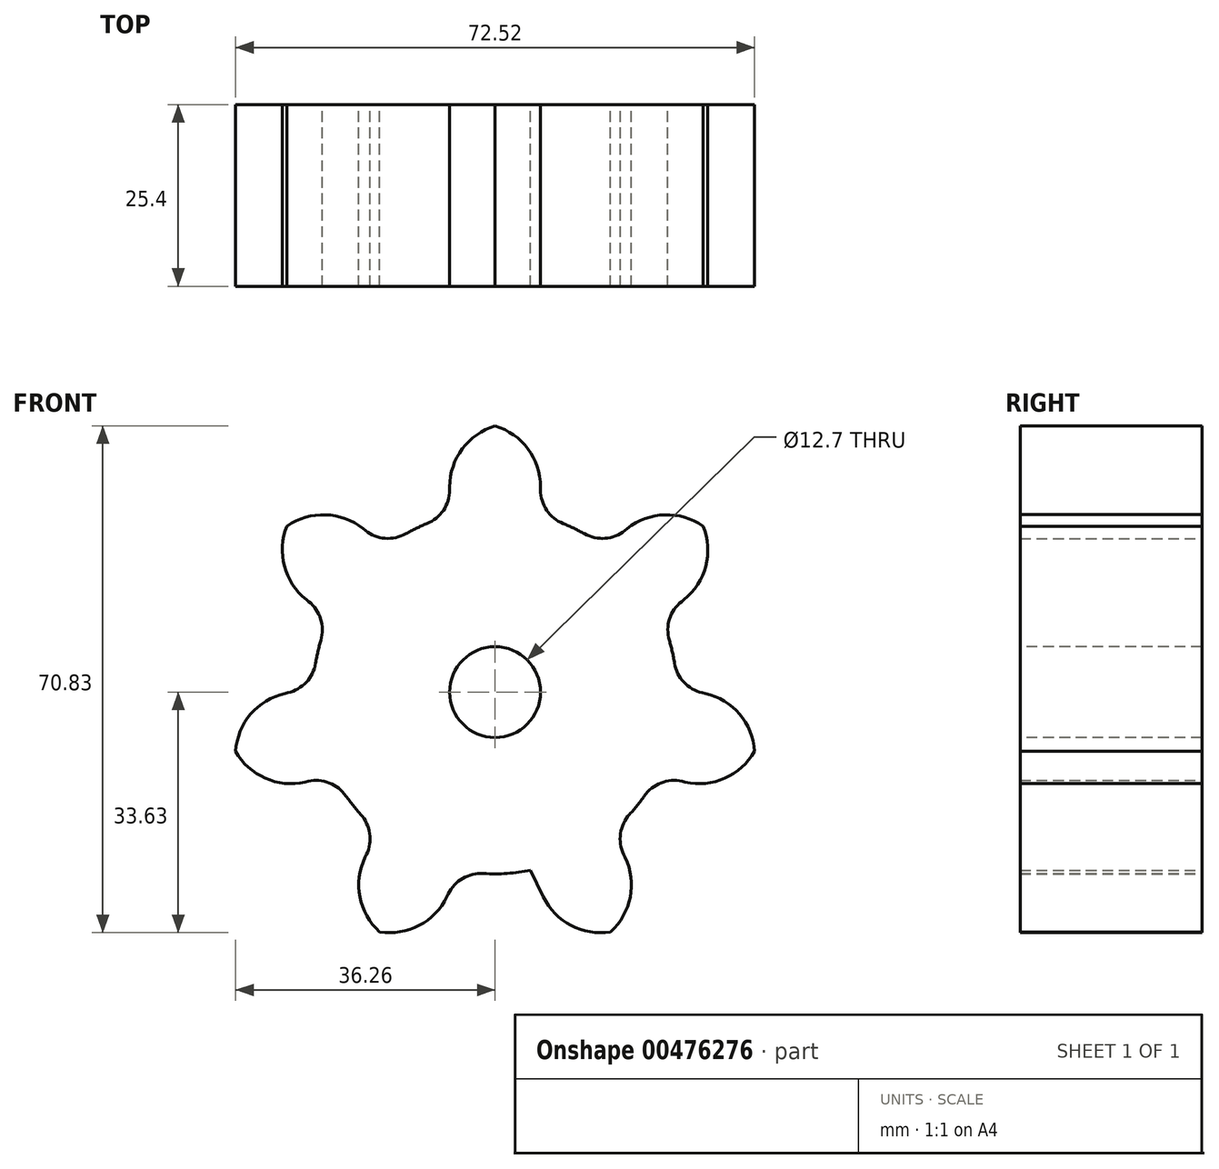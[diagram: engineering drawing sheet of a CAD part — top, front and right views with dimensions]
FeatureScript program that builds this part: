
annotation { "Feature Type Name" : "Feature", "Feature Type Description" : "" }
export const myFeature = defineFeature(function(context is Context, id is Id, definition is map)
    precondition{}
    {
        {
            var Q0;
            Q0=qCreatedBy(makeId("Front.planeOp"),FACE);
            var sketch = newSketch(context, id + "F0", { "sketchPlane" : qUnion([Q0])});
            skCircle(sketch, "E0", {"center": v(0, 0) * mm, "radius": 6.35 * mm});
            skCircle(sketch, "E1", {"center": v(0, 0) * mm, "radius": 25.4 * mm});
            skCircle(sketch, "E2", {"center": v(0, 0) * mm, "radius": 38.1 * mm, "construction": true});
            skLineSegment(sketch, "E3.bottom", {"start": v(-6.35, 37.57) * mm, "end": v(6.35, 37.57) * mm});
            skLineSegment(sketch, "E3.top", {"start": v(-6.35, -37.57) * mm, "end": v(6.35, -37.57) * mm});
            skLineSegment(sketch, "E4", {"start": v(25.41, 28.39) * mm, "end": v(33.33, 18.46) * mm});
            skLineSegment(sketch, "E5", {"start": v(-27.13, -26.75) * mm, "end": v(-34.42, -16.35) * mm});
            skPoint(sketch, "E6.startSnap0", {"position": v(-6.35, 0) * mm});
            skLineSegment(sketch, "E7", {"start": v(-8.92, 1) * mm, "end": v(-1, -8.92) * mm});
            skLineSegment(sketch, "E8", {"start": v(-8.92, 1) * mm, "end": v(25.41, 28.39) * mm});
            skLineSegment(sketch, "E9", {"start": v(-1, -8.92) * mm, "end": v(33.33, 18.46) * mm});
            skLineSegment(sketch, "E10", {"start": v(-6.35, -6.35) * mm, "end": v(6.35, -6.35) * mm});
            skLineSegment(sketch, "E11", {"start": v(6.35, -6.35) * mm, "end": v(6.35, 37.57) * mm});
            skLineSegment(sketch, "E12", {"start": v(-6.35, 37.57) * mm, "end": v(-6.35, -6.35) * mm});
            skLineSegment(sketch, "E13", {"start": v(-4.78, 7.6) * mm, "end": v(38.04, -2.17) * mm});
            skLineSegment(sketch, "E14", {"start": v(38.04, -2.17) * mm, "end": v(35.21, -14.55) * mm});
            skLineSegment(sketch, "E15", {"start": v(35.21, -14.55) * mm, "end": v(-7.6, -4.78) * mm});
            skLineSegment(sketch, "E16", {"start": v(-7.6, -4.78) * mm, "end": v(-4.78, 7.6) * mm});
            skSolve(sketch);
        }
        {
            var Q0;
            Q0=qCreatedBy(makeId("Front.planeOp"),FACE);
            var sketch = newSketch(context, id + "F1", { "sketchPlane" : qUnion([Q0])});
            skCircle(sketch, "E17", {"center": v(0, 0) * mm, "radius": 6.35 * mm});
            skCircle(sketch, "E18", {"center": v(0, 0) * mm, "radius": 38.1 * mm, "construction": true});
            skLineSegment(sketch, "E19", {"start": v(-7.05, 0) * mm, "end": v(10.58, -36.6) * mm});
            skLineSegment(sketch, "E20", {"start": v(10.58, -36.6) * mm, "end": v(22.02, -31.1) * mm});
            skLineSegment(sketch, "E21", {"start": v(22.02, -31.1) * mm, "end": v(2.97, 8.48) * mm});
            skLineSegment(sketch, "E22", {"start": v(2.97, 8.48) * mm, "end": v(-8.48, 2.97) * mm});
            skLineSegment(sketch, "E23", {"start": v(-8.48, 2.97) * mm, "end": v(10.58, -36.6) * mm});
            skLineSegment(sketch, "E24", {"start": v(9.16, 4.38) * mm, "end": v(-10.58, -36.6) * mm});
            skLineSegment(sketch, "E25", {"start": v(-10.58, -36.6) * mm, "end": v(-22.02, -31.1) * mm});
            skLineSegment(sketch, "E26", {"start": v(-22.02, -31.1) * mm, "end": v(-2.97, 8.48) * mm});
            skLineSegment(sketch, "E27", {"start": v(-2.97, 8.48) * mm, "end": v(8.48, 2.97) * mm});
            skLineSegment(sketch, "E28", {"start": v(15.16, -3.05) * mm, "end": v(-35.21, -14.55) * mm});
            skLineSegment(sketch, "E29", {"start": v(-35.21, -14.55) * mm, "end": v(-38.04, -2.17) * mm});
            skLineSegment(sketch, "E30", {"start": v(-38.04, -2.17) * mm, "end": v(12.96, 9.47) * mm});
            skLineSegment(sketch, "E31", {"start": v(12.96, 9.47) * mm, "end": v(15.16, -3.05) * mm});
            skLineSegment(sketch, "E32", {"start": v(12.08, -1.5) * mm, "end": v(-25.41, 28.39) * mm});
            skLineSegment(sketch, "E33", {"start": v(-25.41, 28.39) * mm, "end": v(-33.33, 18.46) * mm});
            skLineSegment(sketch, "E34", {"start": v(-33.33, 18.46) * mm, "end": v(3.34, -10.79) * mm});
            skLineSegment(sketch, "E35", {"start": v(3.34, -10.79) * mm, "end": v(12.08, -1.5) * mm});
            skSolve(sketch);
        }
        {
            var Q0;
            {var subQ5=sQuery(id+"F0.wireOp",EDGE,"E4");Q0=makeQuery(id+"F0.imprint","IMPRINT",FACE,{"disambiguationData":[TD([[makeQuery(id+"F0.imprint","IMPRINT",EDGE,{"derivedFrom":subQ5}),-1.0]])]});}
            var Q1;
            {var subQ5=sQuery(id+"F0.wireOp",EDGE,"E3.bottom");Q1=makeQuery(id+"F0.imprint","IMPRINT",FACE,{"disambiguationData":[TD([[makeQuery(id+"F0.imprint","IMPRINT",EDGE,{"derivedFrom":subQ5}),-1.0]])]});}
            var Q2;
            {var subQ5=sQuery(id+"F0.wireOp",EDGE,"E14");Q2=makeQuery(id+"F0.imprint","IMPRINT",FACE,{"disambiguationData":[TD([[makeQuery(id+"F0.imprint","IMPRINT",EDGE,{"derivedFrom":subQ5}),-1.0]])]});}
            var Q3;
            {var subQ0=sQuery(id+"F0.wireOp",EDGE,"E9");var subQ1=sQuery(id+"F0.wireOp",EDGE,"E1");var subQ2=makeQuery(id+"F0.imprint","INTERSECT",VERTEX,{"derivedFrom":[subQ1,subQ0]});Q3=makeQuery(id+"F0.imprint","IMPRINT",FACE,{"disambiguationData":[TD([[makeQuery(id+"F0.imprint","IMPRINT",EDGE,{"disambiguationData":[TD([[subQ2,1.0]])],"derivedFrom":subQ1}),1.0]])]});}
            var Q4;
            {var subQ0=sQuery(id+"F0.wireOp",EDGE,"E8");var subQ1=sQuery(id+"F0.wireOp",EDGE,"E1");var subQ2=makeQuery(id+"F0.imprint","INTERSECT",VERTEX,{"derivedFrom":[subQ1,subQ0]});Q4=makeQuery(id+"F0.imprint","IMPRINT",FACE,{"disambiguationData":[TD([[makeQuery(id+"F0.imprint","IMPRINT",EDGE,{"disambiguationData":[TD([[subQ2,-1.0]])],"derivedFrom":subQ1}),1.0]])]});}
            var Q5;
            {var subQ1=sQuery(id+"F0.wireOp",EDGE,"E1");var subQ7=sQuery(id+"F0.wireOp",EDGE,"E9");var subQ8=makeQuery(id+"F0.imprint","INTERSECT",VERTEX,{"derivedFrom":[subQ1,subQ7]});Q5=makeQuery(id+"F0.imprint","IMPRINT",FACE,{"disambiguationData":[TD([[makeQuery(id+"F0.imprint","IMPRINT",EDGE,{"disambiguationData":[TD([[subQ8,-1.0]])],"derivedFrom":subQ1}),1.0]])]});}
            var Q6;
            {var subQ0=sQuery(id+"F0.wireOp",EDGE,"E11");var subQ1=sQuery(id+"F0.wireOp",EDGE,"E1");var subQ2=makeQuery(id+"F0.imprint","INTERSECT",VERTEX,{"derivedFrom":[subQ1,subQ0]});Q6=makeQuery(id+"F0.imprint","IMPRINT",FACE,{"disambiguationData":[TD([[makeQuery(id+"F0.imprint","IMPRINT",EDGE,{"disambiguationData":[TD([[subQ2,-1.0]])],"derivedFrom":subQ1}),1.0]])]});}
            var Q7;
            {var subQ0=sQuery(id+"F0.wireOp",EDGE,"E12");var subQ5=sQuery(id+"F0.wireOp",EDGE,"E1");var subQ6=makeQuery(id+"F0.imprint","INTERSECT",VERTEX,{"derivedFrom":[subQ5,subQ0]});Q7=makeQuery(id+"F0.imprint","IMPRINT",FACE,{"disambiguationData":[TD([[makeQuery(id+"F0.imprint","IMPRINT",EDGE,{"disambiguationData":[TD([[subQ6,-1.0]])],"derivedFrom":subQ5}),1.0]])]});}
            var Q8;
            {var subQ6=sQuery(id+"F0.wireOp",EDGE,"E1");var subQ10=sQuery(id+"F0.wireOp",EDGE,"E13");var subQ12=makeQuery(id+"F0.imprint","INTERSECT",VERTEX,{"derivedFrom":[subQ6,subQ10]});Q8=makeQuery(id+"F0.imprint","IMPRINT",FACE,{"disambiguationData":[TD([[makeQuery(id+"F0.imprint","IMPRINT",EDGE,{"disambiguationData":[TD([[subQ12,1.0]])],"derivedFrom":subQ6}),1.0]])]});}
            var Q9;
            Q9=makeQuery(id+"F3.opExtrude","SWEPT_FACE",FACE,{"disambiguationData":[OSD([sQuery(id+"F1.wireOp",EDGE,"E31")])]});
            var Q10;
            Q10=makeQuery(id+"F3.opExtrude","SWEPT_FACE",FACE,{"disambiguationData":[OSD([sQuery(id+"F1.wireOp",EDGE,"E29")])]});
            var Q11;
            {var subQ0=sQuery(id+"F1.wireOp",EDGE,"E28");Q11=makeQuery(id+"F3.opExtrude","SWEPT_FACE",FACE,{"disambiguationData":[OSD([subQ0]),TDD([makeQuery(id+"F1.imprint","IMPRINT",EDGE,{"disambiguationData":[TD([[makeQuery(id+"F1.imprint","INTERSECT",VERTEX,{"derivedFrom":[subQ0,sQuery(id+"F1.wireOp",EDGE,"E29")]}),1.0]])],"derivedFrom":subQ0})])]});}
            var Q12;
            {var subQ0=sQuery(id+"F1.wireOp",EDGE,"E23");Q12=makeQuery(id+"F3.opExtrude","SWEPT_FACE",FACE,{"disambiguationData":[OSD([subQ0]),TDD([makeQuery(id+"F1.imprint","IMPRINT",EDGE,{"disambiguationData":[TD([[makeQuery(id+"F1.imprint","INTERSECT",VERTEX,{"derivedFrom":[sQuery(id+"F1.wireOp",EDGE,"E20"),subQ0]}),1.0]])],"derivedFrom":subQ0})])]});}
            var Q13;
            {var subQ0=sQuery(id+"F1.wireOp",EDGE,"E21");Q13=makeQuery(id+"F3.opExtrude","SWEPT_FACE",FACE,{"disambiguationData":[OSD([subQ0]),TDD([makeQuery(id+"F1.imprint","IMPRINT",EDGE,{"disambiguationData":[TD([[makeQuery(id+"F1.imprint","INTERSECT",VERTEX,{"derivedFrom":[sQuery(id+"F1.wireOp",EDGE,"E20"),subQ0]}),-1.0]])],"derivedFrom":subQ0})])]});}
            var Q14;
            Q14=makeQuery(id+"F3.opExtrude","CAP_FACE",FACE,{"disambiguationData":[OSD([sQuery(id+"F1.wireOp",EDGE,"E20"),sQuery(id+"F1.wireOp",EDGE,"E21"),sQuery(id+"F1.wireOp",EDGE,"E22"),sQuery(id+"F1.wireOp",EDGE,"E23"),sQuery(id+"F1.wireOp",EDGE,"E24"),sQuery(id+"F1.wireOp",EDGE,"E25"),sQuery(id+"F1.wireOp",EDGE,"E26"),sQuery(id+"F1.wireOp",EDGE,"E27"),sQuery(id+"F1.wireOp",EDGE,"E28"),sQuery(id+"F1.wireOp",EDGE,"E29"),sQuery(id+"F1.wireOp",EDGE,"E30"),sQuery(id+"F1.wireOp",EDGE,"E31"),sQuery(id+"F1.wireOp",EDGE,"E32"),sQuery(id+"F1.wireOp",EDGE,"E33"),sQuery(id+"F1.wireOp",EDGE,"E34"),sQuery(id+"F1.wireOp",EDGE,"E35")])],"isStart":false});
            var Q15;
            {var subQ0=sQuery(id+"F1.wireOp",EDGE,"E28");Q15=makeQuery(id+"F3.opExtrude","SWEPT_FACE",FACE,{"disambiguationData":[OSD([subQ0]),TDD([makeQuery(id+"F1.imprint","IMPRINT",EDGE,{"disambiguationData":[TD([[makeQuery(id+"F1.imprint","INTERSECT",VERTEX,{"derivedFrom":[subQ0,sQuery(id+"F1.wireOp",EDGE,"E31")]}),-1.0]])],"derivedFrom":subQ0})])]});}
            var Q16;
            Q16=makeQuery(id+"F3.opExtrude","CAP_FACE",FACE,{"disambiguationData":[OSD([sQuery(id+"F1.wireOp",EDGE,"E20"),sQuery(id+"F1.wireOp",EDGE,"E21"),sQuery(id+"F1.wireOp",EDGE,"E22"),sQuery(id+"F1.wireOp",EDGE,"E23"),sQuery(id+"F1.wireOp",EDGE,"E24"),sQuery(id+"F1.wireOp",EDGE,"E25"),sQuery(id+"F1.wireOp",EDGE,"E26"),sQuery(id+"F1.wireOp",EDGE,"E27"),sQuery(id+"F1.wireOp",EDGE,"E28"),sQuery(id+"F1.wireOp",EDGE,"E29"),sQuery(id+"F1.wireOp",EDGE,"E30"),sQuery(id+"F1.wireOp",EDGE,"E31"),sQuery(id+"F1.wireOp",EDGE,"E32"),sQuery(id+"F1.wireOp",EDGE,"E33"),sQuery(id+"F1.wireOp",EDGE,"E34"),sQuery(id+"F1.wireOp",EDGE,"E35")])],"isStart":true});
            var Q17;
            Q17=makeQuery(id+"F3.opExtrude","SWEPT_FACE",FACE,{"disambiguationData":[OSD([sQuery(id+"F1.wireOp",EDGE,"E20")])]});
            var Q18;
            Q18=makeQuery(id+"F3.opExtrude","SWEPT_FACE",FACE,{"disambiguationData":[OSD([sQuery(id+"F1.wireOp",EDGE,"E25")])]});
            var Q19;
            {var subQ0=sQuery(id+"F1.wireOp",EDGE,"E24");Q19=makeQuery(id+"F3.opExtrude","SWEPT_FACE",FACE,{"disambiguationData":[OSD([subQ0]),TDD([makeQuery(id+"F1.imprint","IMPRINT",EDGE,{"disambiguationData":[TD([[makeQuery(id+"F1.imprint","INTERSECT",VERTEX,{"derivedFrom":[subQ0,sQuery(id+"F1.wireOp",EDGE,"E25")]}),1.0]])],"derivedFrom":subQ0})])]});}
            var Q20;
            {var subQ0=sQuery(id+"F1.wireOp",EDGE,"E26");Q20=makeQuery(id+"F3.opExtrude","SWEPT_FACE",FACE,{"disambiguationData":[OSD([subQ0]),TDD([makeQuery(id+"F1.imprint","IMPRINT",EDGE,{"disambiguationData":[TD([[makeQuery(id+"F1.imprint","INTERSECT",VERTEX,{"derivedFrom":[sQuery(id+"F1.wireOp",EDGE,"E25"),subQ0]}),-1.0]])],"derivedFrom":subQ0})])]});}
            var Q21;
            {var subQ0=sQuery(id+"F0.wireOp",EDGE,"E13");var subQ1=sQuery(id+"F0.wireOp",EDGE,"E0");var subQ2=makeQuery(id+"F0.imprint","INTERSECT",VERTEX,{"derivedFrom":[subQ1,subQ0]});Q21=makeQuery(id+"F0.imprint","IMPRINT",FACE,{"disambiguationData":[TD([[makeQuery(id+"F0.imprint","IMPRINT",EDGE,{"disambiguationData":[TD([[subQ2,-1.0]])],"derivedFrom":subQ1}),-1.0]])]});}
            var Q22;
            {var subQ0=sQuery(id+"F0.wireOp",EDGE,"E8");var subQ1=makeQuery(id+"F0.imprint","INTERSECT",VERTEX,{"derivedFrom":[sQuery(id+"F0.wireOp",EDGE,"E0"),subQ0]});Q22=makeQuery(id+"F0.imprint","IMPRINT",FACE,{"disambiguationData":[TD([[makeQuery(id+"F0.imprint","IMPRINT",EDGE,{"disambiguationData":[TD([[subQ1,1.0]])],"derivedFrom":subQ0}),1.0]])]});}
            var Q23;
            {var subQ0=sQuery(id+"F0.wireOp",EDGE,"E11");var subQ1=sQuery(id+"F0.wireOp",EDGE,"E9");var subQ2=makeQuery(id+"F0.imprint","INTERSECT",VERTEX,{"derivedFrom":[subQ1,subQ0]});Q23=makeQuery(id+"F0.imprint","IMPRINT",FACE,{"disambiguationData":[TD([[makeQuery(id+"F0.imprint","IMPRINT",EDGE,{"disambiguationData":[TD([[subQ2,-1.0]])],"derivedFrom":subQ1}),1.0]])]});}
            var Q24;
            {var subQ0=sQuery(id+"F1.wireOp",EDGE,"E30");Q24=makeQuery(id+"F3.opExtrude","SWEPT_FACE",FACE,{"disambiguationData":[OSD([subQ0]),TDD([makeQuery(id+"F1.imprint","IMPRINT",EDGE,{"disambiguationData":[TD([[makeQuery(id+"F1.imprint","INTERSECT",VERTEX,{"derivedFrom":[subQ0,sQuery(id+"F1.wireOp",EDGE,"E31")]}),1.0]])],"derivedFrom":subQ0})])]});}
            var Q25;
            {var subQ0=sQuery(id+"F1.wireOp",EDGE,"E30");Q25=makeQuery(id+"F3.opExtrude","SWEPT_FACE",FACE,{"disambiguationData":[OSD([subQ0]),TDD([makeQuery(id+"F1.imprint","IMPRINT",EDGE,{"disambiguationData":[TD([[makeQuery(id+"F1.imprint","INTERSECT",VERTEX,{"derivedFrom":[sQuery(id+"F1.wireOp",EDGE,"E29"),subQ0]}),-1.0]])],"derivedFrom":subQ0})])]});}
            var Q26;
            {var subQ0=sQuery(id+"F1.wireOp",EDGE,"E30");Q26=makeQuery(id+"F3.opExtrude","SWEPT_FACE",FACE,{"disambiguationData":[OSD([subQ0]),TDD([makeQuery(id+"F1.imprint","IMPRINT",EDGE,{"disambiguationData":[TD([[makeQuery(id+"F1.imprint","INTERSECT",VERTEX,{"derivedFrom":[sQuery(id+"F1.wireOp",EDGE,"E27"),subQ0]}),-1.0]])],"derivedFrom":subQ0})])]});}
            var Q27;
            {var subQ0=sQuery(id+"F1.wireOp",EDGE,"E32");Q27=makeQuery(id+"F3.opExtrude","SWEPT_FACE",FACE,{"disambiguationData":[OSD([subQ0]),TDD([makeQuery(id+"F1.imprint","IMPRINT",EDGE,{"disambiguationData":[TD([[makeQuery(id+"F1.imprint","INTERSECT",VERTEX,{"derivedFrom":[subQ0,sQuery(id+"F1.wireOp",EDGE,"E33")]}),1.0]])],"derivedFrom":subQ0})])]});}
            var Q28;
            {var subQ0=sQuery(id+"F1.wireOp",EDGE,"E28");Q28=makeQuery(id+"F3.opExtrude","SWEPT_FACE",FACE,{"disambiguationData":[OSD([subQ0]),TDD([makeQuery(id+"F1.imprint","IMPRINT",EDGE,{"disambiguationData":[TD([[makeQuery(id+"F1.imprint","INTERSECT",VERTEX,{"derivedFrom":[sQuery(id+"F1.wireOp",EDGE,"E23"),subQ0]}),1.0]])],"derivedFrom":subQ0})])]});}
            var Q29;
            {var subQ0=sQuery(id+"F1.wireOp",EDGE,"E32");Q29=makeQuery(id+"F3.opExtrude","SWEPT_FACE",FACE,{"disambiguationData":[OSD([subQ0]),TDD([makeQuery(id+"F1.imprint","IMPRINT",EDGE,{"disambiguationData":[TD([[makeQuery(id+"F1.imprint","INTERSECT",VERTEX,{"derivedFrom":[sQuery(id+"F1.wireOp",EDGE,"E27"),subQ0]}),-1.0]])],"derivedFrom":subQ0})])]});}
            var Q30;
            Q30=makeQuery(id+"F3.opExtrude","SWEPT_FACE",FACE,{"disambiguationData":[OSD([sQuery(id+"F1.wireOp",EDGE,"E33")])]});
            var Q31;
            {var subQ0=sQuery(id+"F1.wireOp",EDGE,"E24");Q31=makeQuery(id+"F3.opExtrude","SWEPT_FACE",FACE,{"disambiguationData":[OSD([subQ0]),TDD([makeQuery(id+"F1.imprint","IMPRINT",EDGE,{"disambiguationData":[TD([[makeQuery(id+"F1.imprint","INTERSECT",VERTEX,{"derivedFrom":[subQ0,sQuery(id+"F1.wireOp",EDGE,"E28")]}),-1.0]])],"derivedFrom":subQ0})])]});}
            var Q32;
            {var subQ0=sQuery(id+"F1.wireOp",EDGE,"E24");Q32=makeQuery(id+"F3.opExtrude","SWEPT_FACE",FACE,{"disambiguationData":[OSD([subQ0]),TDD([makeQuery(id+"F1.imprint","IMPRINT",EDGE,{"disambiguationData":[TD([[makeQuery(id+"F1.imprint","INTERSECT",VERTEX,{"derivedFrom":[subQ0,sQuery(id+"F1.wireOp",EDGE,"E27")]}),-1.0]])],"derivedFrom":subQ0}),makeQuery(id+"F1.imprint","IMPRINT",EDGE,{"disambiguationData":[TD([[makeQuery(id+"F1.imprint","INTERSECT",VERTEX,{"derivedFrom":[sQuery(id+"F1.wireOp",EDGE,"E21"),subQ0]}),1.0]])],"derivedFrom":subQ0})])]});}
            var Q33;
            {var subQ0=sQuery(id+"F1.wireOp",EDGE,"E22");Q33=makeQuery(id+"F3.opExtrude","SWEPT_FACE",FACE,{"disambiguationData":[OSD([subQ0]),TDD([makeQuery(id+"F1.imprint","IMPRINT",EDGE,{"disambiguationData":[TD([[makeQuery(id+"F1.imprint","INTERSECT",VERTEX,{"derivedFrom":[subQ0,sQuery(id+"F1.wireOp",EDGE,"E23")]}),1.0]])],"derivedFrom":subQ0})])]});}
            var Q34;
            {var subQ0=sQuery(id+"F1.wireOp",EDGE,"E28");Q34=makeQuery(id+"F3.opExtrude","SWEPT_FACE",FACE,{"disambiguationData":[OSD([subQ0]),TDD([makeQuery(id+"F1.imprint","IMPRINT",EDGE,{"disambiguationData":[TD([[makeQuery(id+"F1.imprint","INTERSECT",VERTEX,{"derivedFrom":[sQuery(id+"F1.wireOp",EDGE,"E21"),subQ0]}),-1.0]])],"derivedFrom":subQ0})])]});}
            var Q35;
            {var subQ0=sQuery(id+"F1.wireOp",EDGE,"E21");Q35=makeQuery(id+"F3.opExtrude","SWEPT_FACE",FACE,{"disambiguationData":[OSD([subQ0]),TDD([makeQuery(id+"F1.imprint","IMPRINT",EDGE,{"disambiguationData":[TD([[makeQuery(id+"F1.imprint","INTERSECT",VERTEX,{"derivedFrom":[subQ0,sQuery(id+"F1.wireOp",EDGE,"E28")]}),-1.0]])],"derivedFrom":subQ0})])]});}
            var Q36;
            Q36=makeQuery(id+"F3.opExtrude","SWEPT_FACE",FACE,{"disambiguationData":[OSD([sQuery(id+"F1.wireOp",EDGE,"E35")])]});
            var Q37;
            {var subQ0=sQuery(id+"F1.wireOp",EDGE,"E27");var subQ1=makeQuery(id+"F1.imprint","INTERSECT",VERTEX,{"derivedFrom":[sQuery(id+"F1.wireOp",EDGE,"E21"),subQ0]});Q37=makeQuery(id+"F3.opExtrude","SWEPT_FACE",FACE,{"disambiguationData":[OSD([subQ0]),TDD([makeQuery(id+"F1.imprint","IMPRINT",EDGE,{"disambiguationData":[TD([[subQ1,1.0]])],"derivedFrom":subQ0}),makeQuery(id+"F1.imprint","IMPRINT",EDGE,{"disambiguationData":[TD([[makeQuery(id+"F1.imprint","INTERSECT",VERTEX,{"derivedFrom":[sQuery(id+"F1.wireOp",EDGE,"E24"),subQ0]}),1.0]])],"derivedFrom":subQ0})])]});}
            var Q38;
            {var subQ0=sQuery(id+"F1.wireOp",EDGE,"E34");Q38=makeQuery(id+"F3.opExtrude","SWEPT_FACE",FACE,{"disambiguationData":[OSD([subQ0]),TDD([makeQuery(id+"F1.imprint","IMPRINT",EDGE,{"disambiguationData":[TD([[makeQuery(id+"F1.imprint","INTERSECT",VERTEX,{"derivedFrom":[sQuery(id+"F1.wireOp",EDGE,"E24"),subQ0]}),1.0]])],"derivedFrom":subQ0})])]});}
            var Q39;
            {var subQ0=sQuery(id+"F1.wireOp",EDGE,"E27");var subQ1=makeQuery(id+"F1.imprint","INTERSECT",VERTEX,{"derivedFrom":[sQuery(id+"F1.wireOp",EDGE,"E22"),subQ0]});Q39=makeQuery(id+"F3.opExtrude","SWEPT_FACE",FACE,{"disambiguationData":[OSD([subQ0]),TDD([makeQuery(id+"F1.imprint","IMPRINT",EDGE,{"disambiguationData":[TD([[makeQuery(id+"F1.imprint","INTERSECT",VERTEX,{"derivedFrom":[sQuery(id+"F1.wireOp",EDGE,"E26"),subQ0]}),-1.0]])],"derivedFrom":subQ0}),makeQuery(id+"F1.imprint","IMPRINT",EDGE,{"disambiguationData":[TD([[subQ1,-1.0]])],"derivedFrom":subQ0})])]});}
            var Q40;
            {var subQ0=sQuery(id+"F1.wireOp",EDGE,"E34");Q40=makeQuery(id+"F3.opExtrude","SWEPT_FACE",FACE,{"disambiguationData":[OSD([subQ0]),TDD([makeQuery(id+"F1.imprint","IMPRINT",EDGE,{"disambiguationData":[TD([[makeQuery(id+"F1.imprint","INTERSECT",VERTEX,{"derivedFrom":[sQuery(id+"F1.wireOp",EDGE,"E23"),subQ0]}),1.0]])],"derivedFrom":subQ0})])]});}
            var Q41;
            {var subQ0=sQuery(id+"F1.wireOp",EDGE,"E26");Q41=makeQuery(id+"F3.opExtrude","SWEPT_FACE",FACE,{"disambiguationData":[OSD([subQ0]),TDD([makeQuery(id+"F1.imprint","IMPRINT",EDGE,{"disambiguationData":[TD([[makeQuery(id+"F1.imprint","INTERSECT",VERTEX,{"derivedFrom":[sQuery(id+"F1.wireOp",EDGE,"E22"),subQ0]}),-1.0]])],"derivedFrom":subQ0}),makeQuery(id+"F1.imprint","IMPRINT",EDGE,{"disambiguationData":[TD([[makeQuery(id+"F1.imprint","INTERSECT",VERTEX,{"derivedFrom":[subQ0,sQuery(id+"F1.wireOp",EDGE,"E27")]}),1.0]])],"derivedFrom":subQ0})])]});}
            var Q42;
            {var subQ0=sQuery(id+"F1.wireOp",EDGE,"E34");Q42=makeQuery(id+"F3.opExtrude","SWEPT_FACE",FACE,{"disambiguationData":[OSD([subQ0]),TDD([makeQuery(id+"F1.imprint","IMPRINT",EDGE,{"disambiguationData":[TD([[makeQuery(id+"F1.imprint","INTERSECT",VERTEX,{"derivedFrom":[sQuery(id+"F1.wireOp",EDGE,"E33"),subQ0]}),-1.0]])],"derivedFrom":subQ0})])]});}
            var Q43;
            {var subQ0=sQuery(id+"F1.wireOp",EDGE,"E26");Q43=makeQuery(id+"F3.opExtrude","SWEPT_FACE",FACE,{"disambiguationData":[OSD([subQ0]),TDD([makeQuery(id+"F1.imprint","IMPRINT",EDGE,{"disambiguationData":[TD([[makeQuery(id+"F1.imprint","INTERSECT",VERTEX,{"derivedFrom":[sQuery(id+"F1.wireOp",EDGE,"E23"),subQ0]}),1.0]])],"derivedFrom":subQ0})])]});}
            var Q44;
            {var subQ0=sQuery(id+"F0.wireOp",EDGE,"E7");var subQ1=sQuery(id+"F0.wireOp",EDGE,"E0");var subQ2=makeQuery(id+"F0.imprint","INTERSECT",VERTEX,{"derivedFrom":[subQ1,subQ0]});Q44=makeQuery(id+"F0.imprint","IMPRINT",FACE,{"disambiguationData":[TD([[makeQuery(id+"F0.imprint","IMPRINT",EDGE,{"disambiguationData":[TD([[subQ2,-1.0]])],"derivedFrom":subQ1}),-1.0]])]});}
            var Q45;
            {var subQ0=sQuery(id+"F0.wireOp",EDGE,"E7");var subQ1=makeQuery(id+"F0.imprint","INTERSECT",VERTEX,{"derivedFrom":[sQuery(id+"F0.wireOp",EDGE,"E0"),subQ0]});Q45=makeQuery(id+"F0.imprint","IMPRINT",FACE,{"disambiguationData":[TD([[makeQuery(id+"F0.imprint","IMPRINT",EDGE,{"disambiguationData":[TD([[subQ1,1.0]])],"derivedFrom":subQ0}),-1.0]])]});}
            var Q46;
            {var subQ0=sQuery(id+"F0.wireOp",EDGE,"E9");var subQ1=makeQuery(id+"F0.imprint","INTERSECT",VERTEX,{"derivedFrom":[sQuery(id+"F0.wireOp",EDGE,"E0"),subQ0]});Q46=makeQuery(id+"F0.imprint","IMPRINT",FACE,{"disambiguationData":[TD([[makeQuery(id+"F0.imprint","IMPRINT",EDGE,{"disambiguationData":[TD([[subQ1,1.0]])],"derivedFrom":subQ0}),-1.0]])]});}
            var Q47;
            {var subQ0=sQuery(id+"F0.wireOp",EDGE,"E8");var subQ1=sQuery(id+"F0.wireOp",EDGE,"E0");var subQ2=makeQuery(id+"F0.imprint","INTERSECT",VERTEX,{"derivedFrom":[subQ1,subQ0]});Q47=makeQuery(id+"F0.imprint","IMPRINT",FACE,{"disambiguationData":[TD([[makeQuery(id+"F0.imprint","IMPRINT",EDGE,{"disambiguationData":[TD([[subQ2,-1.0]])],"derivedFrom":subQ1}),-1.0]])]});}
            var Q48;
            {var subQ0=sQuery(id+"F0.wireOp",EDGE,"E12");var subQ1=sQuery(id+"F0.wireOp",EDGE,"E8");var subQ2=makeQuery(id+"F0.imprint","INTERSECT",VERTEX,{"derivedFrom":[subQ1,subQ0]});Q48=makeQuery(id+"F0.imprint","IMPRINT",FACE,{"disambiguationData":[TD([[makeQuery(id+"F0.imprint","IMPRINT",EDGE,{"disambiguationData":[TD([[subQ2,-1.0]])],"derivedFrom":subQ1}),-1.0]])]});}
            var Q49;
            {var subQ0=sQuery(id+"F0.wireOp",EDGE,"E15");var subQ1=sQuery(id+"F0.wireOp",EDGE,"E7");var subQ2=makeQuery(id+"F0.imprint","INTERSECT",VERTEX,{"derivedFrom":[subQ1,subQ0]});Q49=makeQuery(id+"F0.imprint","IMPRINT",FACE,{"disambiguationData":[TD([[makeQuery(id+"F0.imprint","IMPRINT",EDGE,{"disambiguationData":[TD([[subQ2,-1.0]])],"derivedFrom":subQ1}),1.0]])]});}
            var Q50;
            {var subQ0=sQuery(id+"F0.wireOp",EDGE,"E15");var subQ1=sQuery(id+"F0.wireOp",EDGE,"E7");var subQ2=makeQuery(id+"F0.imprint","INTERSECT",VERTEX,{"derivedFrom":[subQ1,subQ0]});Q50=makeQuery(id+"F0.imprint","IMPRINT",FACE,{"disambiguationData":[TD([[makeQuery(id+"F0.imprint","IMPRINT",EDGE,{"disambiguationData":[TD([[subQ2,-1.0]])],"derivedFrom":subQ1}),-1.0]])]});}
            var Q51;
            {var subQ0=sQuery(id+"F0.wireOp",EDGE,"E9");var subQ1=sQuery(id+"F0.wireOp",EDGE,"E7");var subQ2=makeQuery(id+"F0.imprint","INTERSECT",VERTEX,{"derivedFrom":[subQ1,subQ0]});Q51=makeQuery(id+"F0.imprint","IMPRINT",FACE,{"disambiguationData":[TD([[makeQuery(id+"F0.imprint","IMPRINT",EDGE,{"disambiguationData":[TD([[subQ2,1.0]])],"derivedFrom":subQ1}),1.0]])]});}
            var Q52;
            {var subQ0=sQuery(id+"F0.wireOp",EDGE,"E11");var subQ1=sQuery(id+"F0.wireOp",EDGE,"E0");var subQ2=makeQuery(id+"F0.imprint","INTERSECT",VERTEX,{"derivedFrom":[subQ1,subQ0]});Q52=makeQuery(id+"F0.imprint","IMPRINT",FACE,{"disambiguationData":[TD([[makeQuery(id+"F0.imprint","IMPRINT",EDGE,{"disambiguationData":[TD([[subQ2,1.0]])],"derivedFrom":subQ1}),-1.0]])]});}
            var Q53;
            {var subQ0=sQuery(id+"F0.wireOp",EDGE,"E13");var subQ1=sQuery(id+"F0.wireOp",EDGE,"E0");var subQ2=makeQuery(id+"F0.imprint","INTERSECT",VERTEX,{"derivedFrom":[subQ1,subQ0]});Q53=makeQuery(id+"F0.imprint","IMPRINT",FACE,{"disambiguationData":[TD([[makeQuery(id+"F0.imprint","IMPRINT",EDGE,{"disambiguationData":[TD([[subQ2,1.0]])],"derivedFrom":subQ1}),-1.0]])]});}
            var Q54;
            {var subQ0=sQuery(id+"F0.wireOp",EDGE,"E0");var subQ4=makeQuery(id+"F0.imprint","INTERSECT",VERTEX,{"derivedFrom":[subQ0,sQuery(id+"F0.wireOp",EDGE,"E13")]});Q54=makeQuery(id+"F0.imprint","IMPRINT",FACE,{"disambiguationData":[TD([[makeQuery(id+"F0.imprint","IMPRINT",EDGE,{"disambiguationData":[TD([[subQ4,1.0]])],"derivedFrom":subQ0}),1.0]])]});}
            var Q55;
            {var subQ0=sQuery(id+"F0.wireOp",EDGE,"E16");var subQ1=sQuery(id+"F0.wireOp",EDGE,"E7");var subQ2=makeQuery(id+"F0.imprint","INTERSECT",VERTEX,{"derivedFrom":[subQ1,subQ0]});Q55=makeQuery(id+"F0.imprint","IMPRINT",FACE,{"disambiguationData":[TD([[makeQuery(id+"F0.imprint","IMPRINT",EDGE,{"disambiguationData":[TD([[subQ2,-1.0]])],"derivedFrom":subQ1}),-1.0]])]});}
            var Q56;
            {var subQ0=sQuery(id+"F0.wireOp",EDGE,"E13");var subQ1=sQuery(id+"F0.wireOp",EDGE,"E8");var subQ2=makeQuery(id+"F0.imprint","INTERSECT",VERTEX,{"derivedFrom":[subQ1,subQ0]});Q56=makeQuery(id+"F0.imprint","IMPRINT",FACE,{"disambiguationData":[TD([[makeQuery(id+"F0.imprint","IMPRINT",EDGE,{"disambiguationData":[TD([[subQ2,-1.0]])],"derivedFrom":subQ1}),-1.0]])]});}
            var Q57;
            {var subQ0=sQuery(id+"F1.wireOp",EDGE,"E23");Q57=makeQuery(id+"F3.opExtrude","SWEPT_FACE",FACE,{"disambiguationData":[OSD([subQ0]),TDD([makeQuery(id+"F1.imprint","IMPRINT",EDGE,{"disambiguationData":[TD([[makeQuery(id+"F1.imprint","INTERSECT",VERTEX,{"derivedFrom":[subQ0,sQuery(id+"F1.wireOp",EDGE,"E34")]}),-1.0]])],"derivedFrom":subQ0})])]});}
            var Q58;
            {var subQ0=sQuery(id+"F1.wireOp",EDGE,"E23");Q58=makeQuery(id+"F3.opExtrude","SWEPT_FACE",FACE,{"disambiguationData":[OSD([subQ0]),TDD([makeQuery(id+"F1.imprint","IMPRINT",EDGE,{"disambiguationData":[TD([[makeQuery(id+"F1.imprint","INTERSECT",VERTEX,{"derivedFrom":[sQuery(id+"F1.wireOp",EDGE,"E22"),subQ0]}),-1.0]])],"derivedFrom":subQ0})])]});}
            var Q59;
            {var subQ0=sQuery(id+"F1.wireOp",EDGE,"E22");Q59=makeQuery(id+"F3.opExtrude","SWEPT_FACE",FACE,{"disambiguationData":[OSD([subQ0]),TDD([makeQuery(id+"F1.imprint","IMPRINT",EDGE,{"disambiguationData":[TD([[makeQuery(id+"F1.imprint","INTERSECT",VERTEX,{"derivedFrom":[sQuery(id+"F1.wireOp",EDGE,"E21"),subQ0]}),-1.0]])],"derivedFrom":subQ0})])]});}
            var Q60;
            {var subQ0=sQuery(id+"F1.wireOp",EDGE,"E21");Q60=makeQuery(id+"F3.opExtrude","SWEPT_FACE",FACE,{"disambiguationData":[OSD([subQ0]),TDD([makeQuery(id+"F1.imprint","IMPRINT",EDGE,{"disambiguationData":[TD([[makeQuery(id+"F1.imprint","INTERSECT",VERTEX,{"derivedFrom":[subQ0,sQuery(id+"F1.wireOp",EDGE,"E22")]}),1.0]])],"derivedFrom":subQ0})])]});}
            var Q61;
            {var subQ0=sQuery(id+"F0.wireOp",EDGE,"E15");var subQ1=sQuery(id+"F0.wireOp",EDGE,"E0");var subQ2=makeQuery(id+"F0.imprint","INTERSECT",VERTEX,{"derivedFrom":[subQ1,subQ0]});Q61=makeQuery(id+"F0.imprint","IMPRINT",FACE,{"disambiguationData":[TD([[makeQuery(id+"F0.imprint","IMPRINT",EDGE,{"disambiguationData":[TD([[subQ2,-1.0]])],"derivedFrom":subQ1}),-1.0]])]});}
            var Q62;
            {var subQ0=sQuery(id+"F0.wireOp",EDGE,"E16");var subQ1=sQuery(id+"F0.wireOp",EDGE,"E0");var subQ2=makeQuery(id+"F0.imprint","INTERSECT",VERTEX,{"derivedFrom":[subQ1,subQ0]});Q62=makeQuery(id+"F0.imprint","IMPRINT",FACE,{"disambiguationData":[TD([[makeQuery(id+"F0.imprint","IMPRINT",EDGE,{"disambiguationData":[TD([[subQ2,-1.0]])],"derivedFrom":subQ1}),-1.0]])]});}
            var Q63;
            {var subQ0=sQuery(id+"F0.wireOp",EDGE,"E12");var subQ1=sQuery(id+"F0.wireOp",EDGE,"E0");var subQ2=makeQuery(id+"F0.imprint","INTERSECT",VERTEX,{"derivedFrom":[subQ1,subQ0]});Q63=makeQuery(id+"F0.imprint","IMPRINT",FACE,{"disambiguationData":[TD([[makeQuery(id+"F0.imprint","IMPRINT",EDGE,{"disambiguationData":[TD([[subQ2,-1.0]])],"derivedFrom":subQ1}),-1.0]])]});}
            var Q64;
            {var subQ0=sQuery(id+"F0.wireOp",EDGE,"E15");var subQ1=sQuery(id+"F0.wireOp",EDGE,"E9");var subQ2=makeQuery(id+"F0.imprint","INTERSECT",VERTEX,{"derivedFrom":[subQ1,subQ0]});Q64=makeQuery(id+"F0.imprint","IMPRINT",FACE,{"disambiguationData":[TD([[makeQuery(id+"F0.imprint","IMPRINT",EDGE,{"disambiguationData":[TD([[subQ2,-1.0]])],"derivedFrom":subQ1}),1.0]])]});}
            var Q65;
            {var subQ0=sQuery(id+"F0.wireOp",EDGE,"E10");var subQ1=sQuery(id+"F0.wireOp",EDGE,"E0");var subQ2=makeQuery(id+"F0.imprint","INTERSECT",VERTEX,{"derivedFrom":[subQ1,subQ0]});Q65=makeQuery(id+"F0.imprint","IMPRINT",FACE,{"disambiguationData":[TD([[makeQuery(id+"F0.imprint","IMPRINT",EDGE,{"disambiguationData":[TD([[subQ2,-1.0]])],"derivedFrom":subQ1}),-1.0]])]});}
            var Q66;
            {var subQ0=sQuery(id+"F0.wireOp",EDGE,"E8");var subQ1=sQuery(id+"F0.wireOp",EDGE,"E7");var subQ2=makeQuery(id+"F0.imprint","INTERSECT",VERTEX,{"derivedFrom":[subQ1,subQ0]});Q66=makeQuery(id+"F0.imprint","IMPRINT",FACE,{"disambiguationData":[TD([[makeQuery(id+"F0.imprint","IMPRINT",EDGE,{"disambiguationData":[TD([[subQ2,-1.0]])],"derivedFrom":subQ1}),1.0]])]});}
            var Q67;
            {var subQ0=sQuery(id+"F0.wireOp",EDGE,"E16");var subQ1=sQuery(id+"F0.wireOp",EDGE,"E7");var subQ2=makeQuery(id+"F0.imprint","INTERSECT",VERTEX,{"derivedFrom":[subQ1,subQ0]});Q67=makeQuery(id+"F0.imprint","IMPRINT",FACE,{"disambiguationData":[TD([[makeQuery(id+"F0.imprint","IMPRINT",EDGE,{"disambiguationData":[TD([[subQ2,-1.0]])],"derivedFrom":subQ1}),1.0]])]});}
            extrude(context, id + "F2", {"entities" : qUnion([Q0, Q1, Q2, Q3, Q4, Q5, Q6, Q7, Q8, Q9, Q10, Q11, Q12, Q13, Q14, Q15, Q16, Q17, Q18, Q19, Q20, Q21, Q22, Q23, Q24, Q25, Q26, Q27, Q28, Q29, Q30, Q31, Q32, Q33, Q34, Q35, Q36, Q37, Q38, Q39, Q40, Q41, Q42, Q43, Q44, Q45, Q46, Q47, Q48, Q49, Q50, Q51, Q52, Q53, Q54, Q55, Q56, Q57, Q58, Q59, Q60, Q61, Q62, Q63, Q64, Q65, Q66, Q67]), "depth" : 25.4 * mm});
        }
        {
            var Q0;
            Q0 = qSketchRegion(id + "F1", true);
            extrude(context, id + "F3", {"entities" : qUnion([Q0]), "operationType" : NewBodyOperationType.ADD, "depth" : 25.4 * mm});
        }
        {
            var Q0;
            Q0=makeQuery(id+"F3.opExtrude","SWEPT_EDGE",EDGE,{"disambiguationData":[OSD([sQuery(id+"F1.wireOp",EDGE,"E32"),sQuery(id+"F1.wireOp",EDGE,"E33")])]});
            var Q1;
            Q1=makeQuery(id+"F3.opExtrude","SWEPT_EDGE",EDGE,{"disambiguationData":[OSD([sQuery(id+"F1.wireOp",EDGE,"E33"),sQuery(id+"F1.wireOp",EDGE,"E34")])]});
            var Q2;
            Q2=makeQuery(id+"F2.opExtrude","SWEPT_EDGE",EDGE,{"disambiguationData":[OSD([sQuery(id+"F0.wireOp",EDGE,"E3.bottom"),sQuery(id+"F0.wireOp",EDGE,"E12")])]});
            var Q3;
            Q3=makeQuery(id+"F2.opExtrude","SWEPT_EDGE",EDGE,{"disambiguationData":[OSD([sQuery(id+"F0.wireOp",EDGE,"E3.bottom"),sQuery(id+"F0.wireOp",EDGE,"E11")])]});
            var Q4;
            Q4=makeQuery(id+"F2.opExtrude","SWEPT_EDGE",EDGE,{"disambiguationData":[OSD([sQuery(id+"F0.wireOp",EDGE,"E4"),sQuery(id+"F0.wireOp",EDGE,"E8")])]});
            var Q5;
            Q5=makeQuery(id+"F2.opExtrude","SWEPT_EDGE",EDGE,{"disambiguationData":[OSD([sQuery(id+"F0.wireOp",EDGE,"E4"),sQuery(id+"F0.wireOp",EDGE,"E9")])]});
            var Q6;
            Q6=makeQuery(id+"F2.opExtrude","SWEPT_EDGE",EDGE,{"disambiguationData":[OSD([sQuery(id+"F0.wireOp",EDGE,"E13"),sQuery(id+"F0.wireOp",EDGE,"E14")])]});
            var Q7;
            Q7=makeQuery(id+"F2.opExtrude","SWEPT_EDGE",EDGE,{"disambiguationData":[OSD([sQuery(id+"F0.wireOp",EDGE,"E14"),sQuery(id+"F0.wireOp",EDGE,"E15")])]});
            var Q8;
            Q8=makeQuery(id+"F3.opExtrude","SWEPT_EDGE",EDGE,{"disambiguationData":[OSD([sQuery(id+"F1.wireOp",EDGE,"E20"),sQuery(id+"F1.wireOp",EDGE,"E21")])]});
            var Q9;
            Q9=makeQuery(id+"F3.opExtrude","SWEPT_EDGE",EDGE,{"disambiguationData":[OSD([sQuery(id+"F1.wireOp",EDGE,"E24"),sQuery(id+"F1.wireOp",EDGE,"E25")])]});
            var Q10;
            Q10=makeQuery(id+"F3.opExtrude","SWEPT_EDGE",EDGE,{"disambiguationData":[OSD([sQuery(id+"F1.wireOp",EDGE,"E20"),sQuery(id+"F1.wireOp",EDGE,"E23")])]});
            var Q11;
            Q11=makeQuery(id+"F3.opExtrude","SWEPT_EDGE",EDGE,{"disambiguationData":[OSD([sQuery(id+"F1.wireOp",EDGE,"E25"),sQuery(id+"F1.wireOp",EDGE,"E26")])]});
            var Q12;
            Q12=makeQuery(id+"F3.opExtrude","SWEPT_EDGE",EDGE,{"disambiguationData":[OSD([sQuery(id+"F1.wireOp",EDGE,"E28"),sQuery(id+"F1.wireOp",EDGE,"E29")])]});
            var Q13;
            Q13=makeQuery(id+"F3.opExtrude","SWEPT_EDGE",EDGE,{"disambiguationData":[OSD([sQuery(id+"F1.wireOp",EDGE,"E29"),sQuery(id+"F1.wireOp",EDGE,"E30")])]});
            fillet(context, id + "F4", {"entities" : qUnion([Q0, Q1, Q2, Q3, Q4, Q5, Q6, Q7, Q8, Q9, Q10, Q11, Q12, Q13]), "radius" : 8.9 * mm, "tangentPropagation" : true, "allowEdgeOverflow" : false});
        }
        {
            var Q0;
            Q0=makeQuery(id+"F3.boolean.opBoolean","MERGE",FACE,{"derivedFrom":[makeQuery(id+"F2.opExtrude","CAP_FACE",FACE,{"disambiguationData":[OSD([sQuery(id+"F0.wireOp",EDGE,"E1"),sQuery(id+"F0.wireOp",EDGE,"E3.bottom"),sQuery(id+"F0.wireOp",EDGE,"E4"),sQuery(id+"F0.wireOp",EDGE,"E8"),sQuery(id+"F0.wireOp",EDGE,"E9"),sQuery(id+"F0.wireOp",EDGE,"E11"),sQuery(id+"F0.wireOp",EDGE,"E12"),sQuery(id+"F0.wireOp",EDGE,"E13"),sQuery(id+"F0.wireOp",EDGE,"E14"),sQuery(id+"F0.wireOp",EDGE,"E15")])],"isStart":false}),makeQuery(id+"F3.opExtrude","CAP_FACE",FACE,{"disambiguationData":[OSD([sQuery(id+"F1.wireOp",EDGE,"E20"),sQuery(id+"F1.wireOp",EDGE,"E21"),sQuery(id+"F1.wireOp",EDGE,"E22"),sQuery(id+"F1.wireOp",EDGE,"E23"),sQuery(id+"F1.wireOp",EDGE,"E24"),sQuery(id+"F1.wireOp",EDGE,"E25"),sQuery(id+"F1.wireOp",EDGE,"E26"),sQuery(id+"F1.wireOp",EDGE,"E27"),sQuery(id+"F1.wireOp",EDGE,"E28"),sQuery(id+"F1.wireOp",EDGE,"E29"),sQuery(id+"F1.wireOp",EDGE,"E30"),sQuery(id+"F1.wireOp",EDGE,"E31"),sQuery(id+"F1.wireOp",EDGE,"E32"),sQuery(id+"F1.wireOp",EDGE,"E33"),sQuery(id+"F1.wireOp",EDGE,"E34"),sQuery(id+"F1.wireOp",EDGE,"E35")])],"isStart":false})]});
            var sketch = newSketch(context, id + "F5", { "sketchPlane" : qUnion([Q0])});
            skCircle(sketch, "E36", {"center": v(0, 0) * mm, "radius": 6.35 * mm});
            skSolve(sketch);
        }
        {
            var Q0;
            Q0 = qSketchRegion(id + "F5", true);
            extrude(context, id + "F6", {"entities" : qUnion([Q0]), "operationType" : NewBodyOperationType.REMOVE, "oppositeDirection" : true, "depth" : 25.4 * mm});
        }
        {
            var Q0;
            Q0=makeQuery(id+"F2.opExtrude","SWEPT_EDGE",EDGE,{"disambiguationData":[OSD([sQuery(id+"F0.wireOp",EDGE,"E1"),sQuery(id+"F0.wireOp",EDGE,"E11")])]});
            var Q1;
            Q1=makeQuery(id+"F2.opExtrude","SWEPT_EDGE",EDGE,{"disambiguationData":[OSD([sQuery(id+"F0.wireOp",EDGE,"E1"),sQuery(id+"F0.wireOp",EDGE,"E8")])]});
            var Q2;
            {var subQ0=sQuery(id+"F1.wireOp",EDGE,"E32");var subQ1=sQuery(id+"F0.wireOp",EDGE,"E1");Q2=makeQuery(id+"F3.boolean.opBoolean","INTERSECT",EDGE,{"derivedFrom":[makeQuery(id+"F2.opExtrude","SWEPT_FACE",FACE,{"disambiguationData":[OSD([subQ1]),TDD([makeQuery(id+"F0.imprint","IMPRINT",EDGE,{"disambiguationData":[TD([[makeQuery(id+"F0.imprint","INTERSECT",VERTEX,{"derivedFrom":[subQ1,sQuery(id+"F0.wireOp",EDGE,"E12")]}),-1.0]])],"derivedFrom":subQ1})])]}),makeQuery(id+"F3.opExtrude","SWEPT_FACE",FACE,{"disambiguationData":[OSD([subQ0]),TDD([makeQuery(id+"F1.imprint","IMPRINT",EDGE,{"disambiguationData":[TD([[makeQuery(id+"F1.imprint","INTERSECT",VERTEX,{"derivedFrom":[subQ0,sQuery(id+"F1.wireOp",EDGE,"E33")]}),1.0]])],"derivedFrom":subQ0})])]})]});}
            var Q3;
            Q3=makeQuery(id+"F2.opExtrude","SWEPT_EDGE",EDGE,{"disambiguationData":[OSD([sQuery(id+"F0.wireOp",EDGE,"E1"),sQuery(id+"F0.wireOp",EDGE,"E12")])]});
            var Q4;
            {var subQ0=sQuery(id+"F1.wireOp",EDGE,"E34");var subQ1=sQuery(id+"F0.wireOp",EDGE,"E1");Q4=makeQuery(id+"F3.boolean.opBoolean","INTERSECT",EDGE,{"derivedFrom":[makeQuery(id+"F2.opExtrude","SWEPT_FACE",FACE,{"disambiguationData":[OSD([subQ1]),TDD([makeQuery(id+"F0.imprint","IMPRINT",EDGE,{"disambiguationData":[TD([[makeQuery(id+"F0.imprint","INTERSECT",VERTEX,{"derivedFrom":[subQ1,sQuery(id+"F0.wireOp",EDGE,"E12")]}),-1.0]])],"derivedFrom":subQ1})])]}),makeQuery(id+"F3.opExtrude","SWEPT_FACE",FACE,{"disambiguationData":[OSD([subQ0]),TDD([makeQuery(id+"F1.imprint","IMPRINT",EDGE,{"disambiguationData":[TD([[makeQuery(id+"F1.imprint","INTERSECT",VERTEX,{"derivedFrom":[sQuery(id+"F1.wireOp",EDGE,"E33"),subQ0]}),-1.0]])],"derivedFrom":subQ0})])]})]});}
            var Q5;
            {var subQ0=sQuery(id+"F1.wireOp",EDGE,"E30");var subQ1=sQuery(id+"F0.wireOp",EDGE,"E1");Q5=makeQuery(id+"F3.boolean.opBoolean","INTERSECT",EDGE,{"derivedFrom":[makeQuery(id+"F2.opExtrude","SWEPT_FACE",FACE,{"disambiguationData":[OSD([subQ1]),TDD([makeQuery(id+"F0.imprint","IMPRINT",EDGE,{"disambiguationData":[TD([[makeQuery(id+"F0.imprint","INTERSECT",VERTEX,{"derivedFrom":[subQ1,sQuery(id+"F0.wireOp",EDGE,"E12")]}),-1.0]])],"derivedFrom":subQ1})])]}),makeQuery(id+"F3.opExtrude","SWEPT_FACE",FACE,{"disambiguationData":[OSD([subQ0]),TDD([makeQuery(id+"F1.imprint","IMPRINT",EDGE,{"disambiguationData":[TD([[makeQuery(id+"F1.imprint","INTERSECT",VERTEX,{"derivedFrom":[sQuery(id+"F1.wireOp",EDGE,"E29"),subQ0]}),-1.0]])],"derivedFrom":subQ0})])]})]});}
            var Q6;
            {var subQ0=sQuery(id+"F1.wireOp",EDGE,"E28");var subQ1=sQuery(id+"F0.wireOp",EDGE,"E1");Q6=makeQuery(id+"F3.boolean.opBoolean","INTERSECT",EDGE,{"derivedFrom":[makeQuery(id+"F2.opExtrude","SWEPT_FACE",FACE,{"disambiguationData":[OSD([subQ1]),TDD([makeQuery(id+"F0.imprint","IMPRINT",EDGE,{"disambiguationData":[TD([[makeQuery(id+"F0.imprint","INTERSECT",VERTEX,{"derivedFrom":[subQ1,sQuery(id+"F0.wireOp",EDGE,"E12")]}),-1.0]])],"derivedFrom":subQ1})])]}),makeQuery(id+"F3.opExtrude","SWEPT_FACE",FACE,{"disambiguationData":[OSD([subQ0]),TDD([makeQuery(id+"F1.imprint","IMPRINT",EDGE,{"disambiguationData":[TD([[makeQuery(id+"F1.imprint","INTERSECT",VERTEX,{"derivedFrom":[subQ0,sQuery(id+"F1.wireOp",EDGE,"E29")]}),1.0]])],"derivedFrom":subQ0})])]})]});}
            var Q7;
            {var subQ0=sQuery(id+"F1.wireOp",EDGE,"E26");var subQ1=sQuery(id+"F0.wireOp",EDGE,"E1");Q7=makeQuery(id+"F3.boolean.opBoolean","INTERSECT",EDGE,{"derivedFrom":[makeQuery(id+"F2.opExtrude","SWEPT_FACE",FACE,{"disambiguationData":[OSD([subQ1]),TDD([makeQuery(id+"F0.imprint","IMPRINT",EDGE,{"disambiguationData":[TD([[makeQuery(id+"F0.imprint","INTERSECT",VERTEX,{"derivedFrom":[subQ1,sQuery(id+"F0.wireOp",EDGE,"E12")]}),-1.0]])],"derivedFrom":subQ1})])]}),makeQuery(id+"F3.opExtrude","SWEPT_FACE",FACE,{"disambiguationData":[OSD([subQ0]),TDD([makeQuery(id+"F1.imprint","IMPRINT",EDGE,{"disambiguationData":[TD([[makeQuery(id+"F1.imprint","INTERSECT",VERTEX,{"derivedFrom":[sQuery(id+"F1.wireOp",EDGE,"E25"),subQ0]}),-1.0]])],"derivedFrom":subQ0})])]})]});}
            var Q8;
            {var subQ0=sQuery(id+"F1.wireOp",EDGE,"E24");var subQ1=sQuery(id+"F0.wireOp",EDGE,"E1");Q8=makeQuery(id+"F3.boolean.opBoolean","INTERSECT",EDGE,{"derivedFrom":[makeQuery(id+"F2.opExtrude","SWEPT_FACE",FACE,{"disambiguationData":[OSD([subQ1]),TDD([makeQuery(id+"F0.imprint","IMPRINT",EDGE,{"disambiguationData":[TD([[makeQuery(id+"F0.imprint","INTERSECT",VERTEX,{"derivedFrom":[subQ1,sQuery(id+"F0.wireOp",EDGE,"E12")]}),-1.0]])],"derivedFrom":subQ1})])]}),makeQuery(id+"F3.opExtrude","SWEPT_FACE",FACE,{"disambiguationData":[OSD([subQ0]),TDD([makeQuery(id+"F1.imprint","IMPRINT",EDGE,{"disambiguationData":[TD([[makeQuery(id+"F1.imprint","INTERSECT",VERTEX,{"derivedFrom":[subQ0,sQuery(id+"F1.wireOp",EDGE,"E25")]}),1.0]])],"derivedFrom":subQ0})])]})]});}
            var Q9;
            {var subQ0=sQuery(id+"F1.wireOp",EDGE,"E23");var subQ1=sQuery(id+"F0.wireOp",EDGE,"E1");Q9=makeQuery(id+"F3.boolean.opBoolean","INTERSECT",EDGE,{"derivedFrom":[makeQuery(id+"F2.opExtrude","SWEPT_FACE",FACE,{"disambiguationData":[OSD([subQ1]),TDD([makeQuery(id+"F0.imprint","IMPRINT",EDGE,{"disambiguationData":[TD([[makeQuery(id+"F0.imprint","INTERSECT",VERTEX,{"derivedFrom":[subQ1,sQuery(id+"F0.wireOp",EDGE,"E12")]}),-1.0]])],"derivedFrom":subQ1})])]}),makeQuery(id+"F3.opExtrude","SWEPT_FACE",FACE,{"disambiguationData":[OSD([subQ0]),TDD([makeQuery(id+"F1.imprint","IMPRINT",EDGE,{"disambiguationData":[TD([[makeQuery(id+"F1.imprint","INTERSECT",VERTEX,{"derivedFrom":[sQuery(id+"F1.wireOp",EDGE,"E20"),subQ0]}),1.0]])],"derivedFrom":subQ0})])]})]});}
            var Q10;
            {var subQ0=sQuery(id+"F1.wireOp",EDGE,"E21");var subQ1=sQuery(id+"F0.wireOp",EDGE,"E1");Q10=makeQuery(id+"F3.boolean.opBoolean","INTERSECT",EDGE,{"derivedFrom":[makeQuery(id+"F2.opExtrude","SWEPT_FACE",FACE,{"disambiguationData":[OSD([subQ1]),TDD([makeQuery(id+"F0.imprint","IMPRINT",EDGE,{"disambiguationData":[TD([[makeQuery(id+"F0.imprint","INTERSECT",VERTEX,{"derivedFrom":[subQ1,sQuery(id+"F0.wireOp",EDGE,"E12")]}),-1.0]])],"derivedFrom":subQ1})])]}),makeQuery(id+"F3.opExtrude","SWEPT_FACE",FACE,{"disambiguationData":[OSD([subQ0]),TDD([makeQuery(id+"F1.imprint","IMPRINT",EDGE,{"disambiguationData":[TD([[makeQuery(id+"F1.imprint","INTERSECT",VERTEX,{"derivedFrom":[sQuery(id+"F1.wireOp",EDGE,"E20"),subQ0]}),-1.0]])],"derivedFrom":subQ0})])]})]});}
            var Q11;
            Q11=makeQuery(id+"F2.opExtrude","SWEPT_EDGE",EDGE,{"disambiguationData":[OSD([sQuery(id+"F0.wireOp",EDGE,"E1"),sQuery(id+"F0.wireOp",EDGE,"E15")])]});
            var Q12;
            Q12=makeQuery(id+"F2.opExtrude","SWEPT_EDGE",EDGE,{"disambiguationData":[OSD([sQuery(id+"F0.wireOp",EDGE,"E1"),sQuery(id+"F0.wireOp",EDGE,"E9")])]});
            var Q13;
            Q13=makeQuery(id+"F2.opExtrude","SWEPT_EDGE",EDGE,{"disambiguationData":[OSD([sQuery(id+"F0.wireOp",EDGE,"E1"),sQuery(id+"F0.wireOp",EDGE,"E13")])]});
            fillet(context, id + "F7", {"entities" : qUnion([Q0, Q1, Q2, Q3, Q4, Q5, Q6, Q7, Q8, Q9, Q10, Q11, Q12, Q13]), "radius" : 5.08 * mm, "tangentPropagation" : true, "allowEdgeOverflow" : false});
        }
    });
